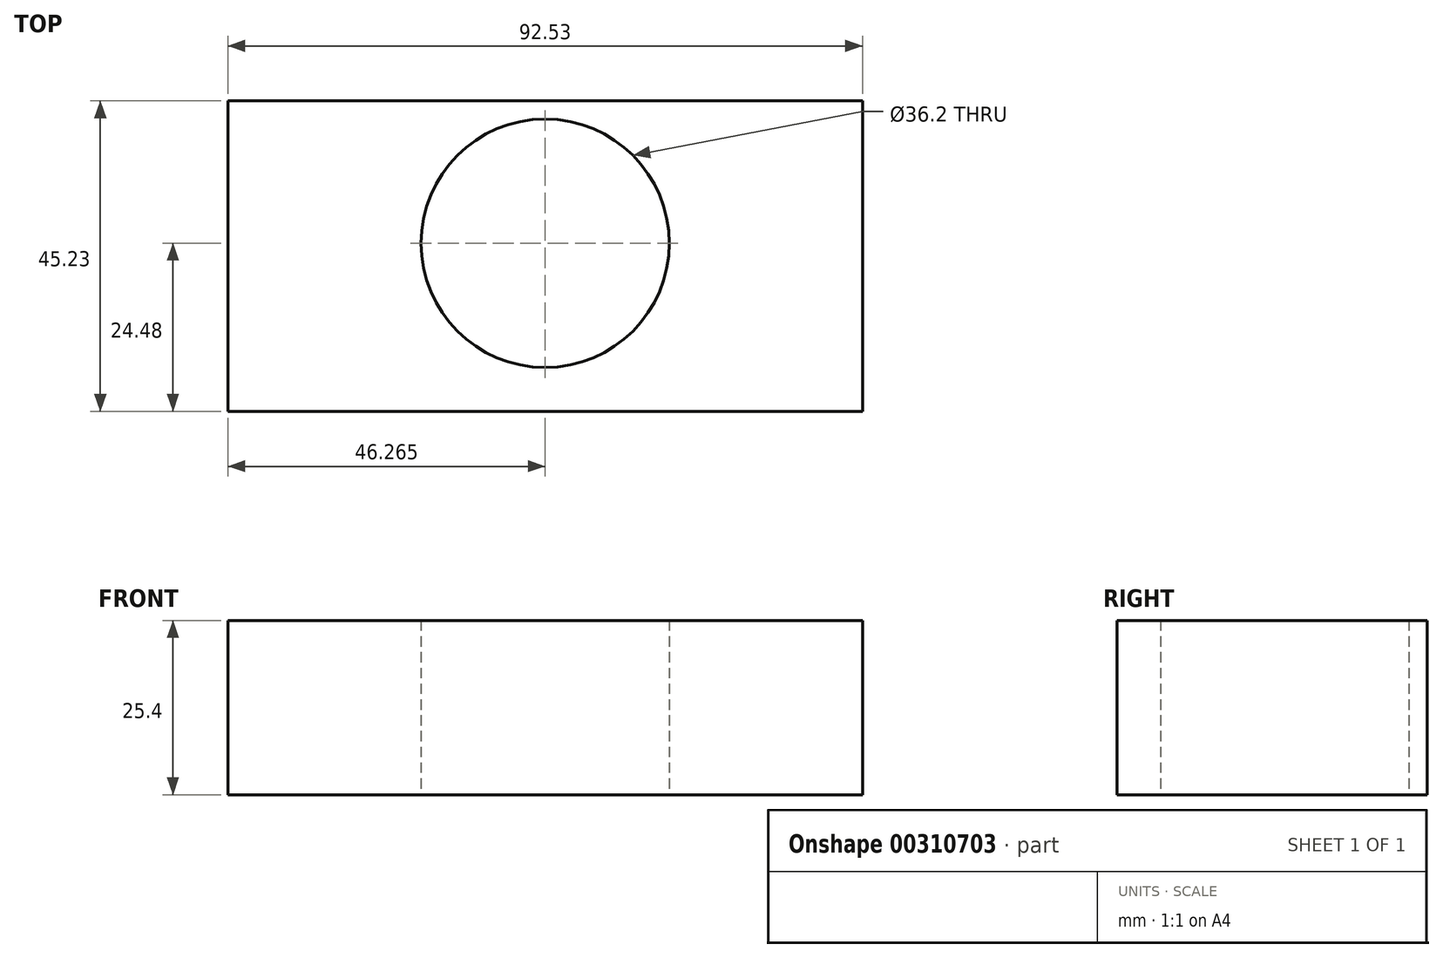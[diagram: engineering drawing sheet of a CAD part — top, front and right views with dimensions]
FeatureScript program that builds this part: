
annotation { "Feature Type Name" : "Feature", "Feature Type Description" : "" }
export const myFeature = defineFeature(function(context is Context, id is Id, definition is map)
    precondition{}
    {
        {
            var Q0;
            Q0=qCreatedBy(makeId("Top.planeOp"),FACE);
            var sketch = newSketch(context, id + "F0", { "sketchPlane" : qUnion([Q0])});
            skLineSegment(sketch, "E0", {"start": v(0, 0) * mm, "end": v(45.85, 0) * mm});
            skLineSegment(sketch, "E1", {"start": v(45.85, 0) * mm, "end": v(45.85, 45.23) * mm});
            skLineSegment(sketch, "E2", {"start": v(45.85, 45.23) * mm, "end": v(-46.68, 45.23) * mm});
            skLineSegment(sketch, "E3", {"start": v(-46.68, 45.23) * mm, "end": v(-46.68, 0) * mm});
            skLineSegment(sketch, "E4", {"start": v(-46.68, 0) * mm, "end": v(0, 0) * mm});
            skCircle(sketch, "E5", {"center": v(-0.41, 24.48) * mm, "radius": 18.1 * mm});
            skPoint(sketch, "E5.centerSnap0", {"position": v(-0.41, 45.23) * mm});
            skSolve(sketch);
        }
        {
            var Q0;
            Q0 = qSketchRegion(id + "F0", true);
            extrude(context, id + "F1", {"entities" : qUnion([Q0]), "depth" : 25.4 * mm});
        }
    });
